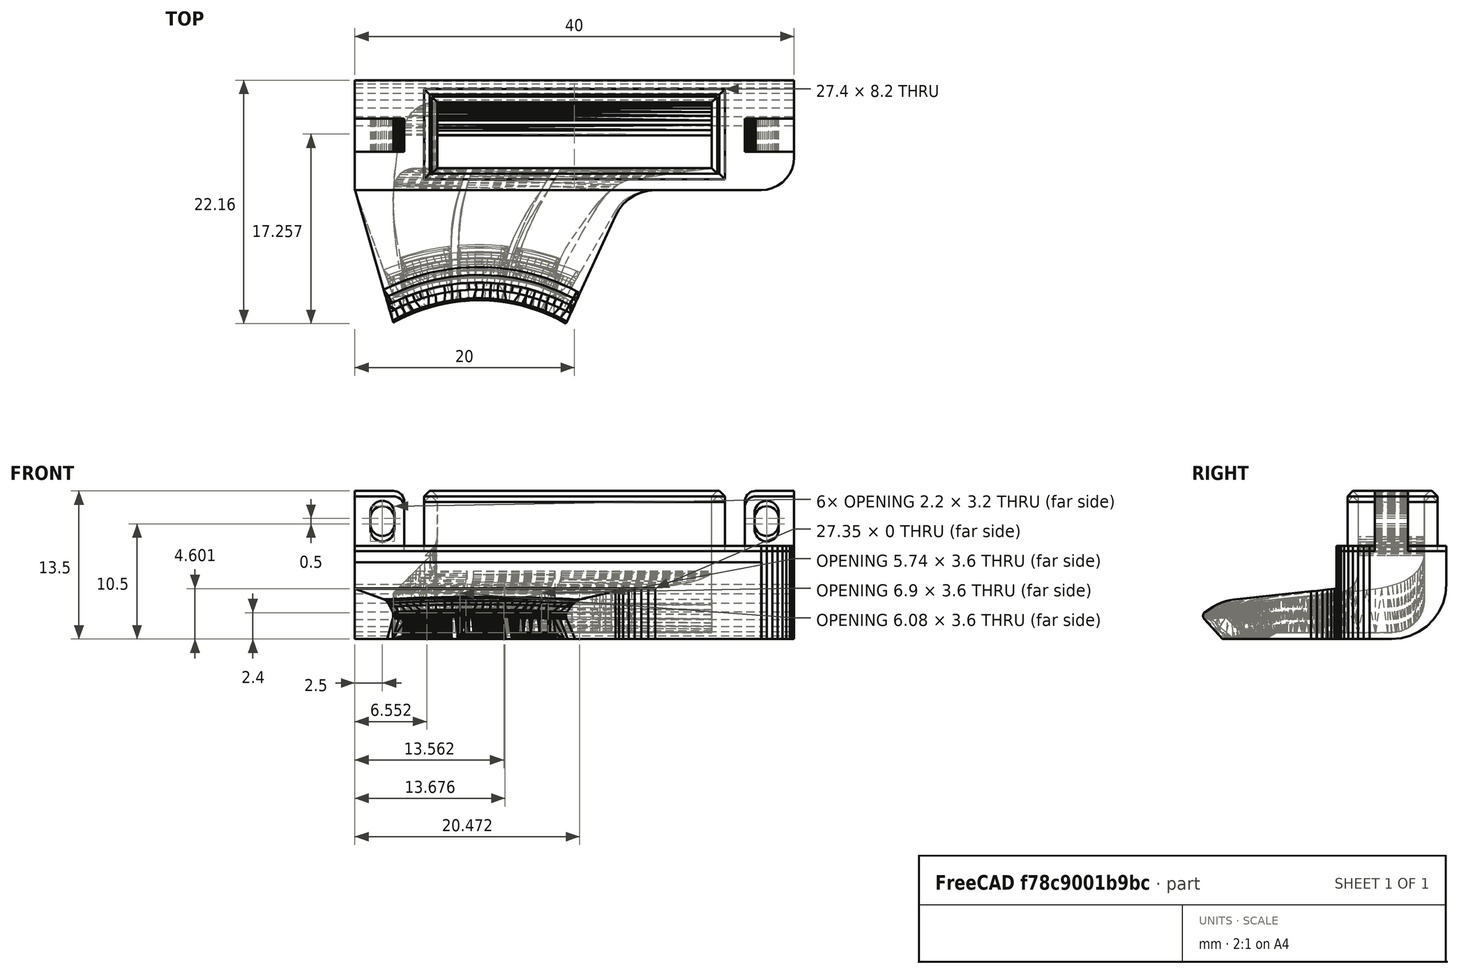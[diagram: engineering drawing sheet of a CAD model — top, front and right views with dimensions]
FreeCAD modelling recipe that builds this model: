
FCSTD DOCUMENT  (FreeCAD 0.18R14555 (Git shallow))
Label: fan-duct
License: All rights reserved
LicenseURL: http://en.wikipedia.org/wiki/All_rights_reserved
objects: Part::Feature×11, Part::Box×4, Mesh::Feature×2, Part::MultiCommon×2, Part::Cut×2, Part::MultiFuse×1
note: 20 computed .brp shape members not serialized (recipe doc carries the construction recipe); baked Part::Feature solids carry a one-line shape summary decoded from their .brp

FEATURE [Mesh::Feature] Fan_Mod_New_Version
FEATURE [Part::Feature] Fan_Mod_New_Version001
  shape: bbox 40 x 22.15 x 13 mm, 3232 faces, 0 solids (baked)
FEATURE [Part::Feature] Fan_Mod_New_Version001001  label="Fan_Mod_New_Version002"
  shape: bbox 40 x 22.15 x 13 mm, 2662 faces, 0 solids (baked)
FEATURE [Part::Feature] Fan_Mod_New_Version001001_solid  label="Fan_Mod_New_Version002 (Solid)"
  Placement = pos=(-135,-131,3) rot=(0,0,1;0rad)
  shape: bbox 40 x 22.15 x 13 mm, 2662 faces (baked)
FEATURE [Part::Box] Box  label="Cube"
  AttacherType = Attacher::AttachEngine3D
  Height = 10
  Length = 42
  Placement = pos=(-7,5.08,0) rot=(0,0,1;0rad)
  Width = 15
FEATURE [Part::Box] Box001  label="Cube001"
  AttacherType = Attacher::AttachEngine3D
  Height = 10
  Length = 42
  Placement = pos=(-7,5.08,0) rot=(0,0,1;0rad)
  Width = 15
FEATURE [Part::Feature] Fan_Mod_New_Version001001_solid001  label="Fan_Mod_New_Version002 (Solid)001"
  Placement = pos=(-135,-131,3) rot=(0,0,1;0rad)
  shape: bbox 40 x 22.15 x 13 mm, 2662 faces (baked)
FEATURE [Part::MultiCommon] Common
  Shapes = -> [Box,Fan_Mod_New_Version001001_solid]
FEATURE [Mesh::Feature] noozle_80  label="noozle-80"
FEATURE [Part::Feature] noozle_80001
  shape: bbox 37.04 x 9.725 x 7 mm, 2300 faces, 0 solids (baked)
FEATURE [Part::Feature] noozle_80001001  label="noozle_80002"
  shape: bbox 37.04 x 9.725 x 7 mm, 2142 faces, 0 solids (baked)
FEATURE [Part::Feature] noozle_80001001_solid  label="noozle-80-solid"
  Placement = pos=(13.52,15.22,3) rot=(0,0,1;0rad)
  shape: bbox 37.04 x 9.725 x 7 mm, 2142 faces (baked)
FEATURE [Part::Cut] Cut
  Base = -> Fan_Mod_New_Version001001_solid001
  Tool = -> Box001
FEATURE [Part::Feature] Cut001
  shape: bbox 40 x 10 x 13 mm, 559 faces (baked)
FEATURE [Part::Feature] Cut002
  shape: bbox 40 x 10 x 13 mm, 559 faces (baked)
FEATURE [Part::Box] Box002  label="Cube002"
  AttacherType = Attacher::AttachEngine3D
  Height = 10
  Length = 43
  Placement = pos=(-6,18,10.6) rot=(0,0,1;0rad)
  Width = 14
FEATURE [Part::Box] Box003  label="Cube003"
  AttacherType = Attacher::AttachEngine3D
  Height = 10
  Length = 43
  Placement = pos=(-6,18,10.1) rot=(0,0,1;0rad)
  Width = 14
FEATURE [Part::MultiCommon] Common001  label="top"
  Placement = pos=(0,0,0.5) rot=(0,0,1;0rad)
  Shapes = -> [Cut001,Box003]
FEATURE [Part::Cut] Cut003  label="bottom"
  Base = -> Cut002
  Tool = -> Box002
FEATURE [Part::MultiFuse] Fusion
  Shapes = -> [Cut003,Common001,noozle_80001001_solid]
FEATURE [Part::Feature] Fusion001
  shape: bbox 40 x 19.72 x 13.5 mm, 2721 faces (baked)
FEATURE [Part::Feature] Fusion001_solid  label="Fusion001 (Solid)"
  shape: bbox 40 x 19.72 x 13.5 mm, 2721 faces (baked)
